# Revit family: 318_717dcb15b8024070a2688602c5a2ae
name_source: partatom
category: Pipe Accessories
units: mm (PartAtom-declared; Revit-internal decimal feet)

## family parameters
Always vertical = Yes
Cut with Voids When Loaded = No
Part Type = Valve - Normal
Round Connector Dimension = Use Diameter
Shared = No
Work Plane-Based = No

## types (1)
- FAR-3875 34
    B = 32 mm  [stored 0.104987 ft]
    B1 = 11 mm  [stored 0.0360892 ft]
    B1__ve = -11 mm  [stored -0.0360892 ft]
    B2 = 21 mm  [stored 0.0688976 ft]
    B2__ve = -21 mm  [stored -0.0688976 ft]
    BP = 20 mm
    C1 = 23 mm
    CAT0 = Yes
    CenSd_R_6 = 16 mm
    Description = MULTIFAR 3/4" chr. lockshield manifold m-f, 2 ports m24x19
    E1 = 21 mm  [stored 0.0688976 ft]
    E1__ve = -21 mm  [stored -0.0688976 ft]
    E2 = 4 mm  [stored 0.0131234 ft]
    E2__ve = -4 mm
    E3 = 13 mm
    E3__ve = -13 mm
    L = 94 mm  [stored 0.308399 ft]
    L1 = 12 mm  [stored 0.0393701 ft]
    L1__ve = -12 mm  [stored -0.0393701 ft]
    L2 = 3 mm  [stored 0.00984252 ft]
    L3 = 80 mm
    L3__ve = -80 mm
    L4 = 10 mm  [stored 0.0328084 ft]
    L4__ve = -10 mm  [stored -0.0328084 ft]
    L5 = 40 mm
    MP1 = 20 mm
    MP2 = 20 mm
    Manufacturer = FAR
    QmdConnectorList = 301;MP1;302;MP2;303;BP;304;BP
    R = 18 mm  [stored 0.0590551 ft]
    R1 = 10 mm  [stored 0.0328084 ft]
    R10 = 14 mm  [stored 0.0459318 ft]
    R11 = 14 mm  [stored 0.0459318 ft]
    R13 = 11 mm  [stored 0.0360892 ft]
    R3 = 14 mm  [stored 0.0459318 ft]
    R4 = 10 mm  [stored 0.0328084 ft]
    R6 = 11 mm  [stored 0.0360892 ft]
    R8 = 10 mm  [stored 0.0328084 ft]
    URL = www.far.eu
    magiPartTypeId = 318
    magiProductCode = FAR-3875 34
    magiProductFamilyId = 717dcb15b8024070a2688602c5a2ae
    magiProductId = 717dcb15b8024070a2688602c5a2ae

note: [stored X ft] marks values corroborated as IEEE doubles in the binary element streams (Revit-internal decimal feet)

## geometry (parser evidence)
native form markers: Sweep x2
no freeform markers — native parametric forms only
